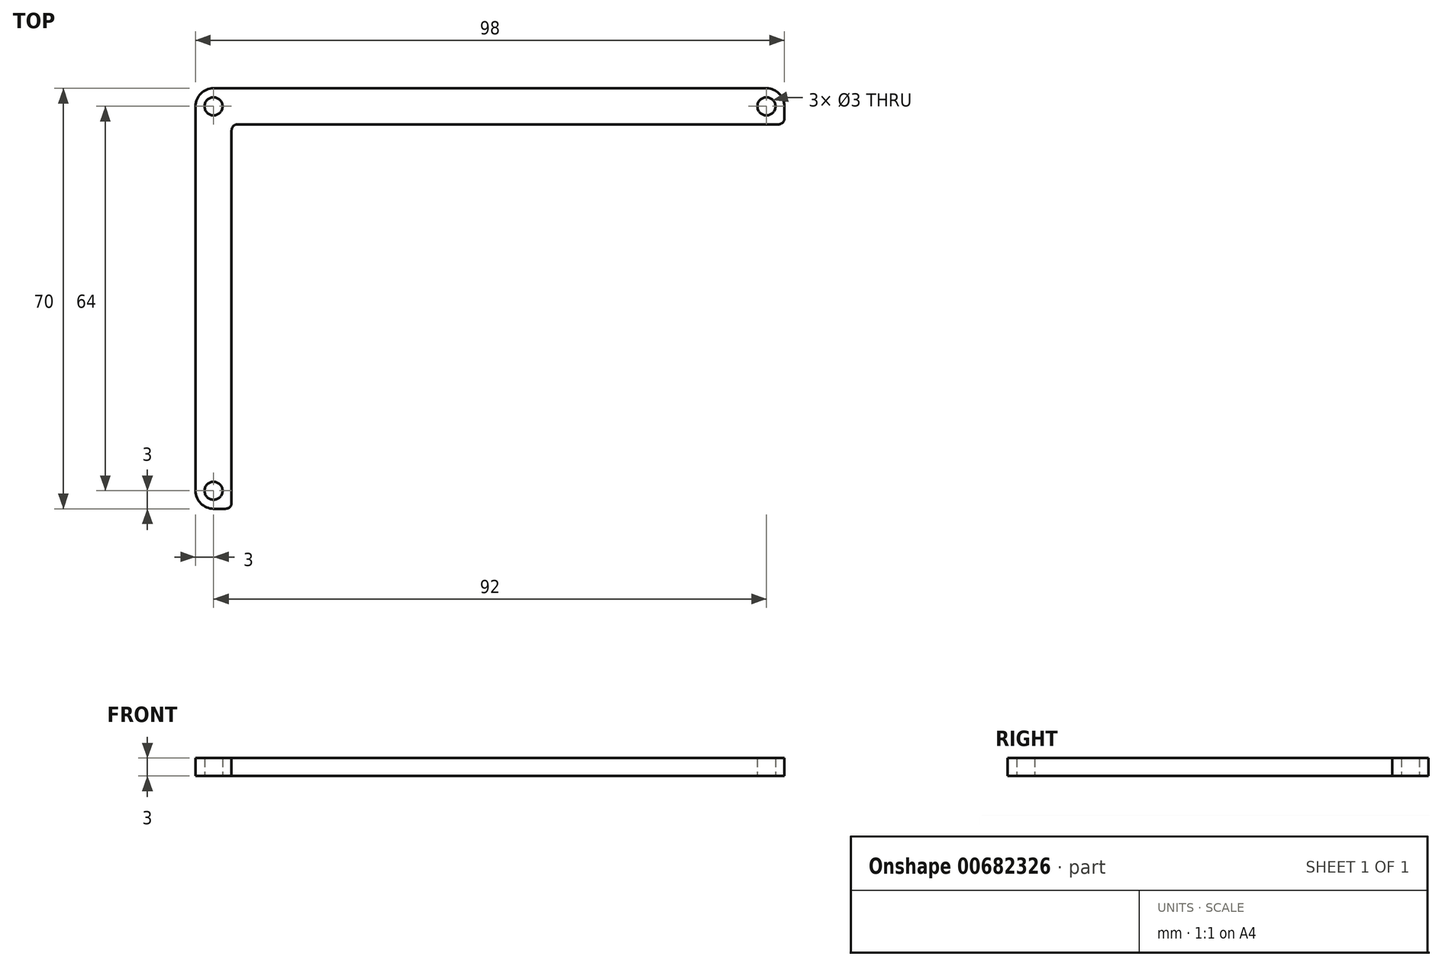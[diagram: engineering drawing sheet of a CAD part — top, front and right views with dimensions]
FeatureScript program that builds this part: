
annotation { "Feature Type Name" : "Feature", "Feature Type Description" : "" }
export const myFeature = defineFeature(function(context is Context, id is Id, definition is map)
    precondition{}
    {
        {
            var Q0;
            Q0=qCreatedBy(makeId("Top.planeOp"),FACE);
            var sketch = newSketch(context, id + "F0", { "sketchPlane" : qUnion([Q0])});
            skLineSegment(sketch, "E0.bottom", {"start": v(7, 0) * mm, "end": v(97, 0) * mm});
            skLineSegment(sketch, "E0.top", {"start": v(3, 6) * mm, "end": v(95, 6) * mm});
            skLineSegment(sketch, "E0.left", {"start": v(0, 1) * mm, "end": v(0, 3) * mm});
            skLineSegment(sketch, "E0.right", {"start": v(98, 1) * mm, "end": v(98, 3) * mm});
            skPoint(sketch, "E1.visualSharp", {"position": v(0, 6) * mm});
            skArc(sketch, "E1.filletArc", {"start": v(3, 6) * mm, "mid": v(0.88, 5.12) * mm, "end": v(0, 3) * mm});
            skPoint(sketch, "E2.visualSharp", {"position": v(98, 6) * mm});
            skArc(sketch, "E2.filletArc", {"start": v(98, 3) * mm, "mid": v(97.12, 5.12) * mm, "end": v(95, 6) * mm});
            skPoint(sketch, "E3.visualSharp", {"position": v(0, 0) * mm});
            skPoint(sketch, "E4.visualSharp", {"position": v(98, 0) * mm});
            skArc(sketch, "E4.filletArc", {"start": v(97, 0) * mm, "mid": v(97.7, 0.3) * mm, "end": v(98, 1) * mm});
            skCircle(sketch, "E5", {"center": v(3, 3) * mm, "radius": 1.5 * mm});
            skCircle(sketch, "E6", {"center": v(95, 3) * mm, "radius": 1.5 * mm});
            skLineSegment(sketch, "E7.top", {"start": v(3, -64) * mm, "end": v(5, -64) * mm});
            skLineSegment(sketch, "E7.left", {"start": v(0, 0) * mm, "end": v(0, -61) * mm});
            skLineSegment(sketch, "E7.right", {"start": v(6, -1) * mm, "end": v(6, -63) * mm});
            skPoint(sketch, "E8.visualSharp", {"position": v(0, -64) * mm});
            skArc(sketch, "E8.filletArc", {"start": v(0, -61) * mm, "mid": v(0.88, -63.12) * mm, "end": v(3, -64) * mm});
            skPoint(sketch, "E9.visualSharp", {"position": v(6, -64) * mm});
            skArc(sketch, "E9.filletArc", {"start": v(5, -64) * mm, "mid": v(5.7, -63.7) * mm, "end": v(6, -63) * mm});
            skArc(sketch, "E10.filletArc", {"start": v(7, 0) * mm, "mid": v(6.3, -0.3) * mm, "end": v(6, -1) * mm});
            skLineSegment(sketch, "E11", {"start": v(0, 0) * mm, "end": v(0, 1) * mm});
            skCircle(sketch, "E12", {"center": v(3, -61) * mm, "radius": 1.5 * mm});
            skSolve(sketch);
        }
        {
            var Q0;
            Q0 = qSketchRegion(id + "F0", true);
            extrude(context, id + "F1", {"entities" : qUnion([Q0]), "depth" : 3 * mm, "offsetDistance" : 25 * mm});
        }
    });
